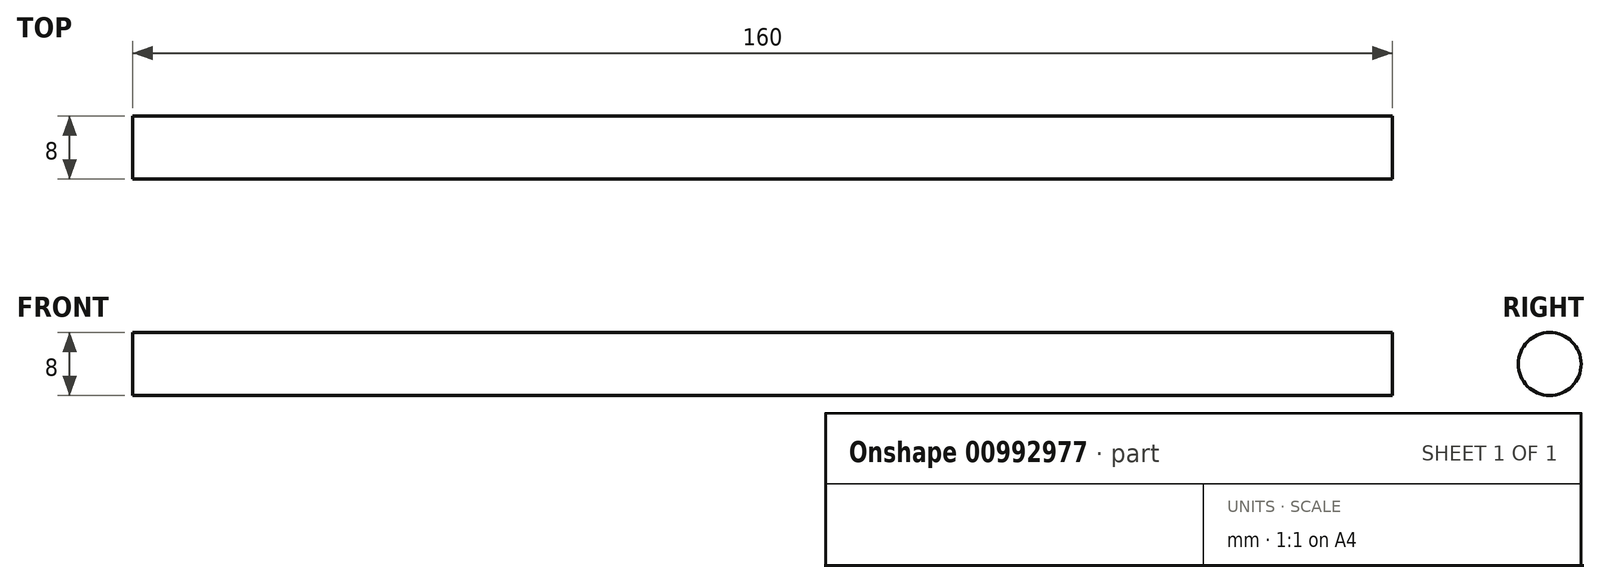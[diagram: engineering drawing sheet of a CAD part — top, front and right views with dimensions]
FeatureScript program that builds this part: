
annotation { "Feature Type Name" : "Feature", "Feature Type Description" : "" }
export const myFeature = defineFeature(function(context is Context, id is Id, definition is map)
    precondition{}
    {
        {
            var Q0;
            Q0=qCreatedBy(makeId("Right.planeOp"),FACE);
            var sketch = newSketch(context, id + "F0", { "sketchPlane" : qUnion([Q0])});
            skCircle(sketch, "E0", {"center": v(0, 0) * mm, "radius": 4 * mm});
            skSolve(sketch);
        }
        {
            var Q0;
            Q0 = qSketchRegion(id + "F0", true);
            extrude(context, id + "F1", {"entities" : qUnion([Q0]), "endBound" : BoundingType.SYMMETRIC, "depth" : 160 * mm, "offsetDistance" : 25 * mm});
        }
    });
